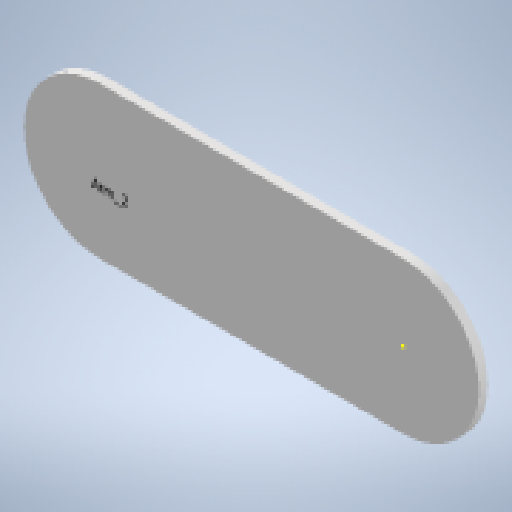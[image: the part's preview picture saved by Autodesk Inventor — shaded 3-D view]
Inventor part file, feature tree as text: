
AUTODESK INVENTOR PART (.ipt)
format: ipt  version: 2023 (Build 270158000, 158)  size: 138,240 bytes
history: native  units: mm
features: sketch x3, extrude x2, other x1
ambient origin geometry x8: Origin, YZ Plane, XZ Plane, XY Plane, X Axis, Y Axis, Z Axis, Center Point
bodies: Body1 (feature_tree)
feature tree (6):
  other  "實體1"
  extrude  "擠出1"  Depth=50.0mm
  sketch  "草圖2"
  extrude  "擠出2"  Depth=200.0mm
  sketch  "草圖1"
  sketch  "草圖3"
